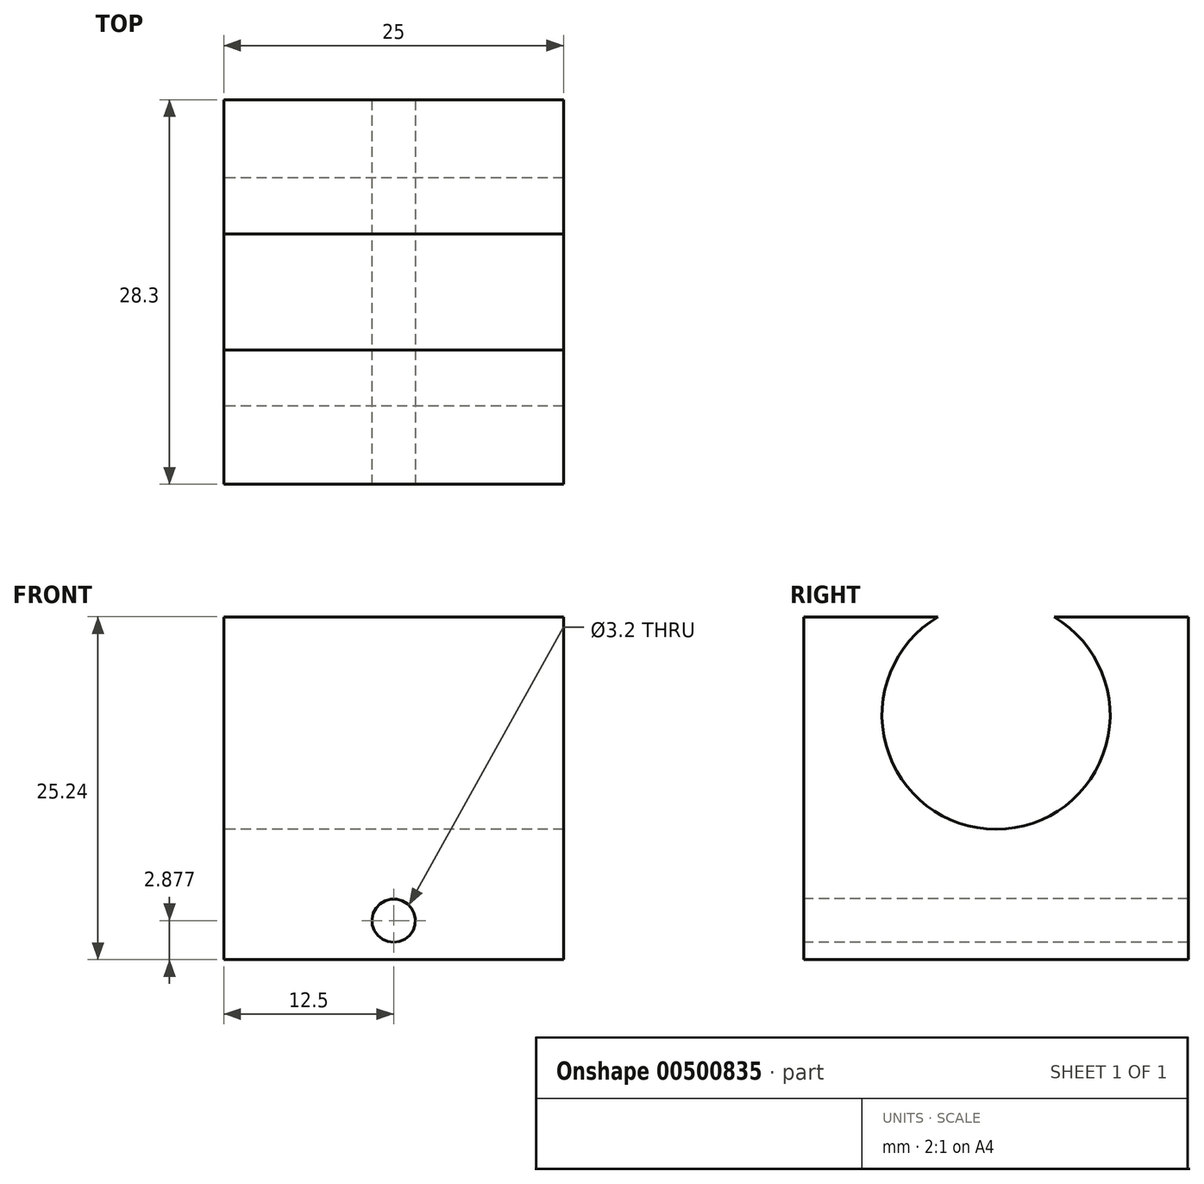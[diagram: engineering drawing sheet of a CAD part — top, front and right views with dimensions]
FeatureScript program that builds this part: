
annotation { "Feature Type Name" : "Feature", "Feature Type Description" : "" }
export const myFeature = defineFeature(function(context is Context, id is Id, definition is map)
    precondition{}
    {
        {
            var Q0;
            Q0=qCreatedBy(makeId("Right.planeOp"),FACE);
            var sketch = newSketch(context, id + "F0", { "sketchPlane" : qUnion([Q0])});
            skPoint(sketch, "E0", {"position": v(-0.56, -5) * mm});
            skLineSegment(sketch, "E1", {"start": v(-0.56, -5) * mm, "end": v(6.37, -5) * mm, "construction": true});
            skLineSegment(sketch, "E2", {"start": v(-0.56, -5) * mm, "end": v(-0.56, -8.25) * mm, "construction": true});
            skArc(sketch, "E3", {"start": v(-3.68, 17.07) * mm, "mid": v(0.6, 1.44) * mm, "end": v(4.86, 17.08) * mm});
            skLineSegment(sketch, "E4", {"start": v(-13.56, -8.16) * mm, "end": v(14.74, -8.16) * mm});
            skLineSegment(sketch, "E5", {"start": v(-13.56, 17.07) * mm, "end": v(-3.68, 17.07) * mm});
            skLineSegment(sketch, "E6", {"start": v(4.86, 17.08) * mm, "end": v(14.74, 17.08) * mm});
            skLineSegment(sketch, "E7", {"start": v(-13.56, 17.07) * mm, "end": v(-13.56, -8.16) * mm});
            skLineSegment(sketch, "E8", {"start": v(14.74, 17.08) * mm, "end": v(14.74, -8.16) * mm});
            skSolve(sketch);
        }
        {
            var Q0;
            Q0 = qSketchRegion(id + "F0", true);
            extrude(context, id + "F1", {"entities" : qUnion([Q0]), "depth" : 25 * mm, "offsetDistance" : 25 * mm});
        }
        {
            var Q0;
            Q0=makeQuery(id+"F1.opExtrude","SWEPT_FACE",FACE,{"disambiguationData":[OSD([sQuery(id+"F0.wireOp",EDGE,"E7")])]});
            var sketch = newSketch(context, id + "F2", { "sketchPlane" : qUnion([Q0])});
            skLineSegment(sketch, "E9", {"start": v(0, -5.28) * mm, "end": v(25, -5.28) * mm, "construction": true});
            skCircle(sketch, "E10", {"center": v(12.5, -5.28) * mm, "radius": 1.6 * mm});
            skSolve(sketch);
        }
        {
            var Q0;
            Q0 = qSketchRegion(id + "F2", true);
            extrude(context, id + "F3", {"entities" : qUnion([Q0]), "operationType" : NewBodyOperationType.REMOVE, "oppositeDirection" : true, "depth" : 32 * mm, "offsetDistance" : 25 * mm});
        }
    });
